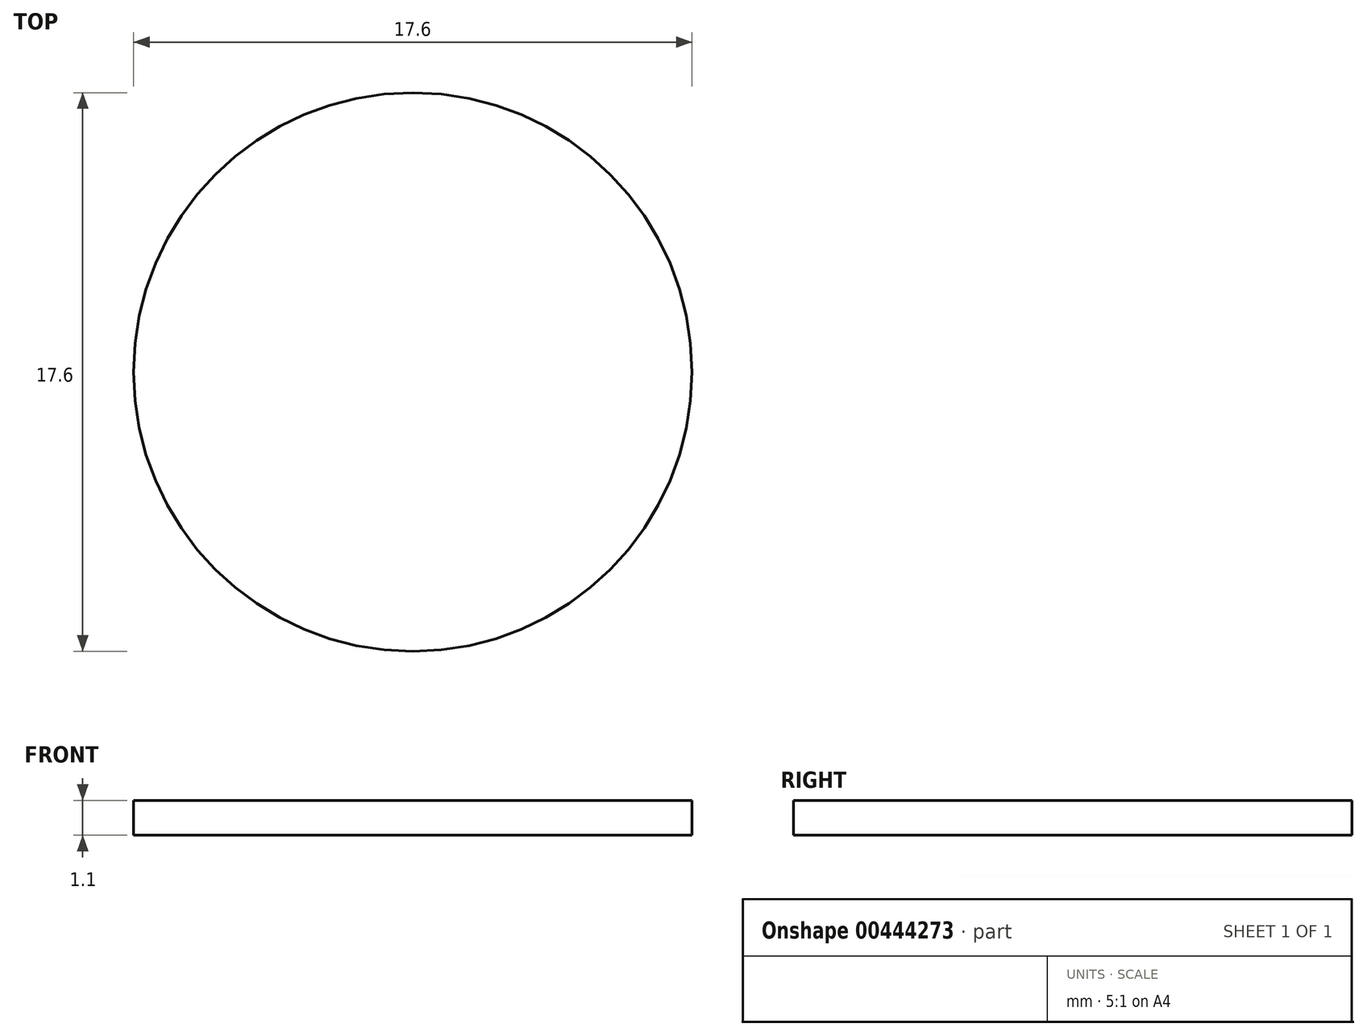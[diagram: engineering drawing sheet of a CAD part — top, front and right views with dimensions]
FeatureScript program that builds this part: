
annotation { "Feature Type Name" : "Feature", "Feature Type Description" : "" }
export const myFeature = defineFeature(function(context is Context, id is Id, definition is map)
    precondition{}
    {
        {
            var Q0;
            Q0=qCreatedBy(makeId("Top.planeOp"),FACE);
            var sketch = newSketch(context, id + "F0", { "sketchPlane" : qUnion([Q0])});
            skCircle(sketch, "E0", {"center": v(0, 0) * mm, "radius": 8.8 * mm});
            skSolve(sketch);
        }
        {
            var Q0;
            Q0 = qSketchRegion(id + "F0", true);
            extrude(context, id + "F1", {"entities" : qUnion([Q0]), "depth" : 1.1 * mm});
        }
    });
